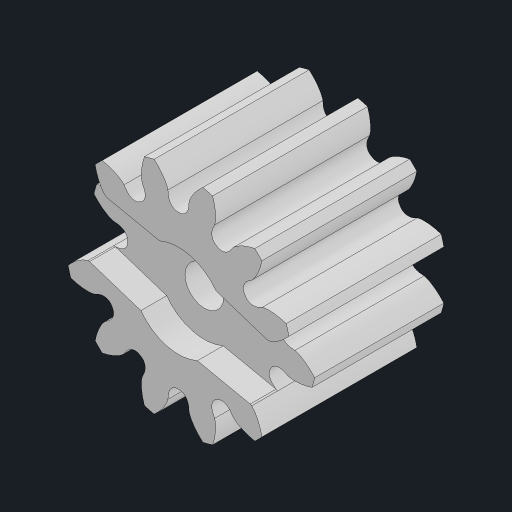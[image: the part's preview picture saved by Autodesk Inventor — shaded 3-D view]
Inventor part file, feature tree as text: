
AUTODESK INVENTOR PART (.ipt)
format: ipt  version: 2023.2 (Build 272271030, 271C)  size: 794,112 bytes
history: native  units: mm
features: sketch x3, extrude x3, reference x3, other x3, pattern_circular x1, hole x1, projected_geometry x1
ambient origin geometry x8: Origin, YZ Plane, XZ Plane, XY Plane, X Axis, Y Axis, Z Axis, Center Point
bodies: Solid1 (feature_tree)
feature tree (15):
  sketch  "Sketch1"  dims[d0=10.0mm d1=0.0mm d2=0.0mm d3=0.0mm]
  extrude  "Extrusion1"  TaperAngle=0.0deg  [1 undecoded]
  extrude  "Extrusion2"  Depth=0.15mm
  pattern_circular  "Circular Pattern1"  [2 undecoded]
  extrude  "Extrusion3"  Depth=6.0mm
  hole  "Hole2"  [1 undecoded]
  sketch  "Sketch3"  dims[d4=120.0mm d5=360.0deg d17=0.15mm]
  projected_geometry  "Projected Loop1"
  reference  "Reference1"
  reference  "Reference2"
  reference  "Reference3"
  sketch  "Sketch4"  dims[d18=0.15mm d19=0.15mm d20=0.15mm d21=0.15mm d22=2.0mm d23=0.0mm d24=3.0mm d25=6.0mm d26=8.0mm d27=8.0mm d28=90.0deg d29=8.0mm d30=20.594885mm]
  other  "<userpath>\OneDrive\Documents\Inventor\Battlebots\Walking Leg Test.iam"
  other  "Walking Leg Test.iam"
  other  "SG90 - Micro Servo 9g - Tower Pro:2"
note: 4 required parameter values undecoded (feature->parameter linkage not recoverable at this tier; creation-order binding heuristic only, values carry confidence <= 0.55)
